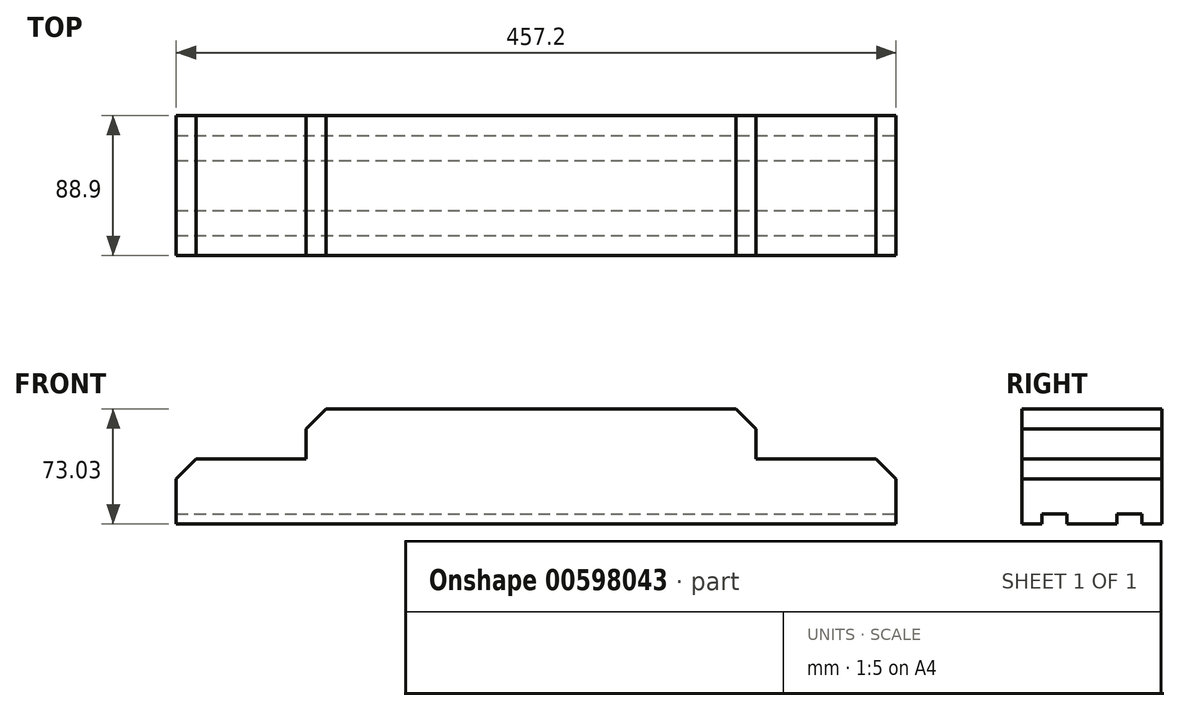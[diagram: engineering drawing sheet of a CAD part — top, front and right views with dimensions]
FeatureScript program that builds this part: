
annotation { "Feature Type Name" : "Feature", "Feature Type Description" : "" }
export const myFeature = defineFeature(function(context is Context, id is Id, definition is map)
    precondition{}
    {
        {
            var Q0;
            Q0=qCreatedBy(makeId("Front.planeOp"),FACE);
            var sketch = newSketch(context, id + "F0", { "sketchPlane" : qUnion([Q0])});
            skLineSegment(sketch, "E0.bottom", {"start": v(228.6, 20.64) * mm, "end": v(139.7, 20.64) * mm});
            skLineSegment(sketch, "E0.top", {"start": v(228.6, -20.64) * mm, "end": v(-228.6, -20.64) * mm});
            skLineSegment(sketch, "E0.left", {"start": v(228.6, 20.64) * mm, "end": v(228.6, -20.64) * mm});
            skLineSegment(sketch, "E0.right", {"start": v(-228.6, 20.64) * mm, "end": v(-228.6, -20.64) * mm});
            skPoint(sketch, "E0.middle", {"position": v(0, 0) * mm});
            skLineSegment(sketch, "E1", {"start": v(-146.05, 52.39) * mm, "end": v(-146.05, 20.64) * mm});
            skLineSegment(sketch, "E2", {"start": v(-146.05, 52.39) * mm, "end": v(139.7, 52.39) * mm});
            skLineSegment(sketch, "E3", {"start": v(139.7, 52.39) * mm, "end": v(139.7, 20.64) * mm});
            skLineSegment(sketch, "E4.trimOffspring", {"start": v(-146.05, 20.64) * mm, "end": v(-228.6, 20.64) * mm});
            skSolve(sketch);
        }
        {
            var Q0;
            Q0 = qSketchRegion(id + "F0", true);
            extrude(context, id + "F1", {"entities" : qUnion([Q0]), "endBound" : BoundingType.SYMMETRIC, "depth" : 88.9 * mm, "offsetDistance" : 25.4 * mm});
        }
        {
            var Q0;
            Q0=makeQuery(id+"F1.opExtrude","SWEPT_EDGE",EDGE,{"disambiguationData":[OSD([sQuery(id+"F0.wireOp",EDGE,"E1"),sQuery(id+"F0.wireOp",EDGE,"E2")])]});
            var Q1;
            Q1=makeQuery(id+"F1.opExtrude","SWEPT_EDGE",EDGE,{"disambiguationData":[OSD([sQuery(id+"F0.wireOp",EDGE,"E0.right"),sQuery(id+"F0.wireOp",EDGE,"E4.trimOffspring")])]});
            var Q2;
            Q2=makeQuery(id+"F1.opExtrude","SWEPT_EDGE",EDGE,{"disambiguationData":[OSD([sQuery(id+"F0.wireOp",EDGE,"E2"),sQuery(id+"F0.wireOp",EDGE,"E3")])]});
            var Q3;
            Q3=makeQuery(id+"F1.opExtrude","SWEPT_EDGE",EDGE,{"disambiguationData":[OSD([sQuery(id+"F0.wireOp",EDGE,"E0.bottom"),sQuery(id+"F0.wireOp",EDGE,"E0.left")])]});
            chamfer(context, id + "F2", {"entities" : qUnion([Q0, Q1, Q2, Q3]), "width" : 12.7 * mm, "tangentPropagation" : true});
        }
        {
            var Q0;
            Q0=qCreatedBy(makeId("Right.planeOp"),FACE);
            var sketch = newSketch(context, id + "F3", { "sketchPlane" : qUnion([Q0])});
            skPoint(sketch, "E5.middle", {"position": v(0, 0) * mm});
            skLineSegment(sketch, "E6", {"start": v(-31.75, -14.29) * mm, "end": v(-31.75, -20.64) * mm});
            skLineSegment(sketch, "E7", {"start": v(-31.75, -14.29) * mm, "end": v(-15.88, -14.29) * mm});
            skLineSegment(sketch, "E8", {"start": v(-15.88, -14.29) * mm, "end": v(-15.88, -20.64) * mm});
            skLineSegment(sketch, "E9", {"start": v(31.75, -14.29) * mm, "end": v(31.75, -20.64) * mm});
            skLineSegment(sketch, "E10", {"start": v(31.75, -14.29) * mm, "end": v(15.88, -14.29) * mm});
            skLineSegment(sketch, "E11", {"start": v(15.88, -14.29) * mm, "end": v(15.88, -20.64) * mm});
            skLineSegment(sketch, "E12", {"start": v(-31.75, -20.64) * mm, "end": v(-15.88, -20.64) * mm});
            skLineSegment(sketch, "E13", {"start": v(15.88, -20.64) * mm, "end": v(31.75, -20.64) * mm});
            skSolve(sketch);
        }
        {
            var Q0;
            Q0 = qSketchRegion(id + "F3", true);
            extrude(context, id + "F4", {"entities" : qUnion([Q0]), "operationType" : NewBodyOperationType.REMOVE, "endBound" : BoundingType.SYMMETRIC, "oppositeDirection" : true, "depth" : 482.6 * mm, "offsetDistance" : 25.4 * mm});
        }
    });
